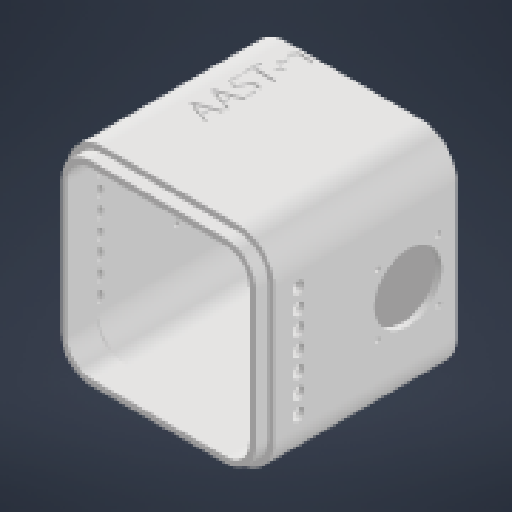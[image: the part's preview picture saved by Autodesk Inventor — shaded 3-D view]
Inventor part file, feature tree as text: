
AUTODESK INVENTOR PART (.ipt)
format: ipt  version: 2024 (Build 280153000, 153)  size: 915,968 bytes
history: native  units: mm
features: extrude x8, sketch x7, other x1, shell x1, chamfer x1
ambient origin geometry x8: Origin, YZ Plane, XZ Plane, XY Plane, X Axis, Y Axis, Z Axis, Center Point
bodies: Body1 (feature_tree)
feature tree (18):
  other  "솔리드1"
  extrude  "돌출1"  Depth=170.0mm
  shell  "쉘1"  Thickness=170.0mm
  sketch  "스케치2"
  extrude  "돌출2"  Depth=30.0mm
  chamfer  "모따기1"  Distance=30.0mm
  extrude  "돌출3"  Depth=30.0mm
  extrude  "돌출4"  Depth=150.0mm TaperAngle=0.0deg
  extrude  "돌출5"  Depth=5.0mm
  extrude  "돌출6"  Depth=170.0mm
  extrude  "돌출7"  Depth=170.0mm
  extrude  "돌출8"  Depth=30.0mm
  sketch  "스케치1"
  sketch  "스케치3"
  sketch  "스케치4"
  sketch  "스케치6"
  sketch  "스케치7"
  sketch  "스케치8"
